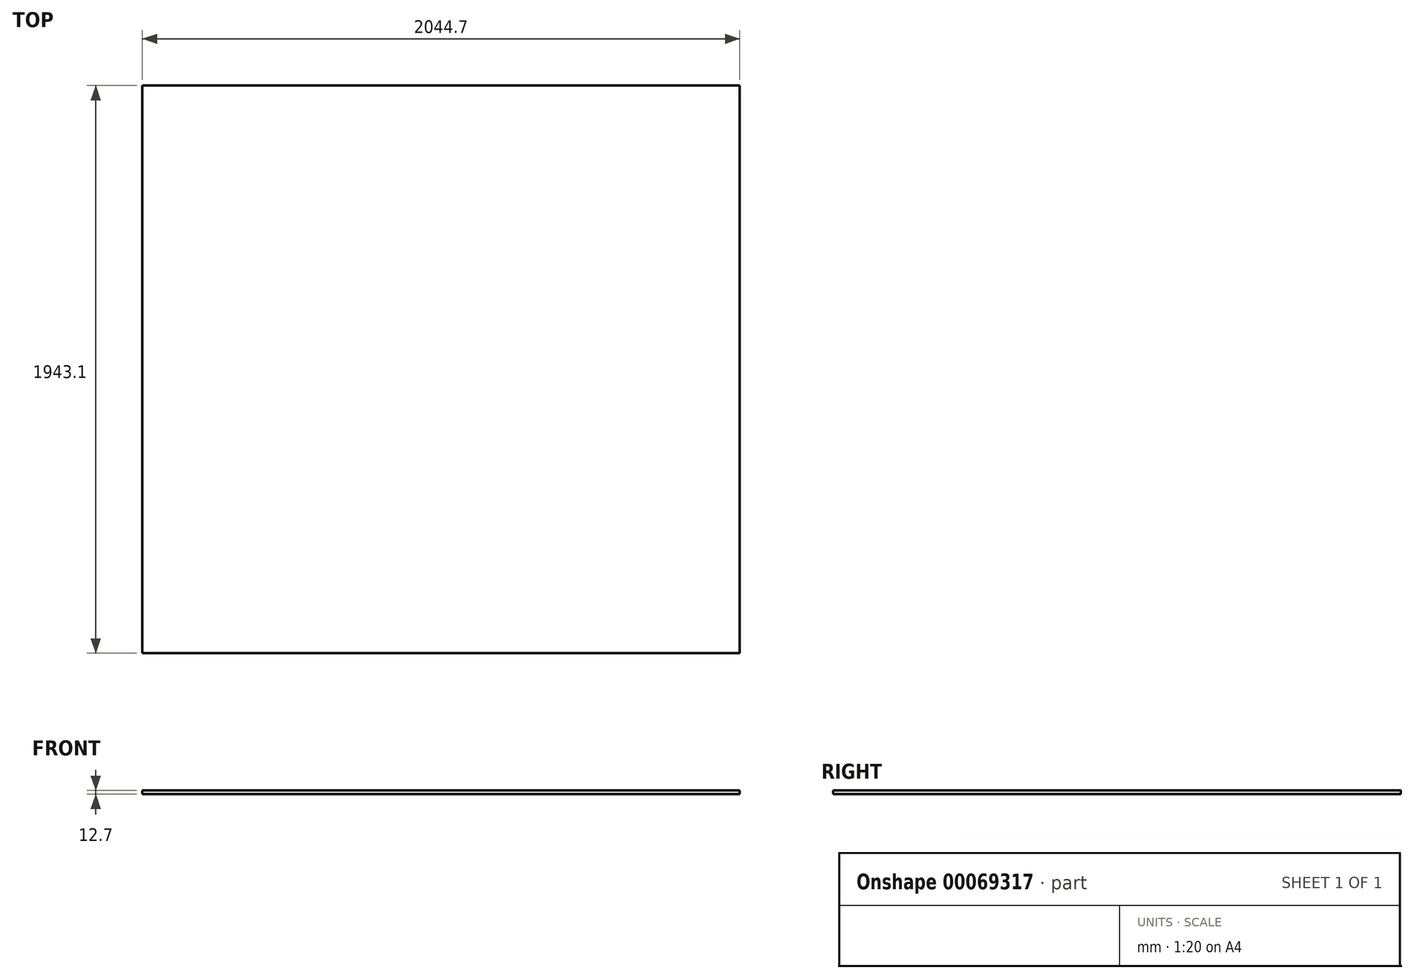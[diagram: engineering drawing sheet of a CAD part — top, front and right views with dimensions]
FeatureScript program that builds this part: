
annotation { "Feature Type Name" : "Feature", "Feature Type Description" : "" }
export const myFeature = defineFeature(function(context is Context, id is Id, definition is map)
    precondition{}
    {
        {
            var Q0;
            Q0=qCreatedBy(makeId("Top.planeOp"),FACE);
            var sketch = newSketch(context, id + "F0", { "sketchPlane" : qUnion([Q0])});
            skLineSegment(sketch, "E0.rect.bottom", {"start": v(1022.35, -971.55) * mm, "end": v(-1022.35, -971.55) * mm});
            skLineSegment(sketch, "E0.rect.top", {"start": v(1022.35, 971.55) * mm, "end": v(-1022.35, 971.55) * mm});
            skLineSegment(sketch, "E0.rect.left", {"start": v(1022.35, -971.55) * mm, "end": v(1022.35, 971.55) * mm});
            skLineSegment(sketch, "E0.rect.right", {"start": v(-1022.35, -971.55) * mm, "end": v(-1022.35, 971.55) * mm});
            skPoint(sketch, "E0.rect.middle", {"position": v(0, 0) * mm});
            skSolve(sketch);
        }
        {
            var Q0;
            Q0 = qSketchRegion(id + "F0", true);
            extrude(context, id + "F1", {"entities" : qUnion([Q0]), "depth" : 12.7 * mm});
        }
    });
